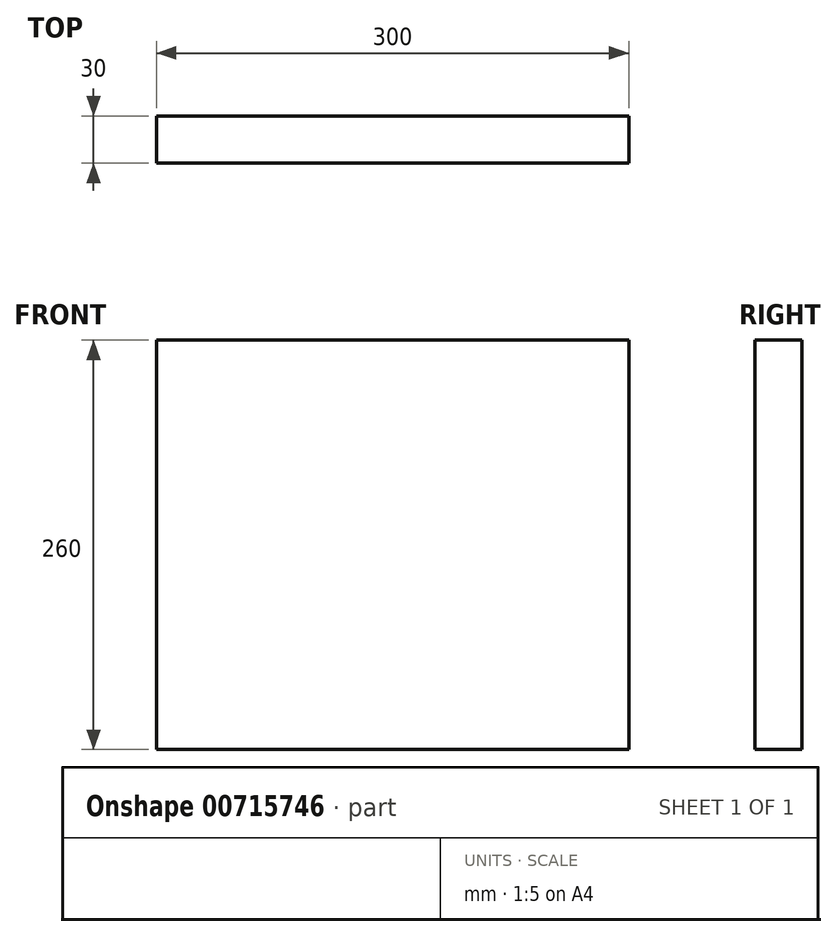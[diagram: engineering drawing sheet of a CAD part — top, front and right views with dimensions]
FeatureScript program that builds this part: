
annotation { "Feature Type Name" : "Feature", "Feature Type Description" : "" }
export const myFeature = defineFeature(function(context is Context, id is Id, definition is map)
    precondition{}
    {
        {
            var Q0;
            Q0=qCreatedBy(makeId("Front.planeOp"),FACE);
            var sketch = newSketch(context, id + "F0", { "sketchPlane" : qUnion([Q0])});
            skLineSegment(sketch, "E0.bottom", {"start": v(-150, 130) * mm, "end": v(150, 130) * mm});
            skLineSegment(sketch, "E0.top", {"start": v(-150, -130) * mm, "end": v(150, -130) * mm});
            skLineSegment(sketch, "E0.left", {"start": v(-150, 130) * mm, "end": v(-150, -130) * mm});
            skLineSegment(sketch, "E0.right", {"start": v(150, 130) * mm, "end": v(150, -130) * mm});
            skSolve(sketch);
        }
        {
            var Q0;
            Q0 = qSketchRegion(id + "F0", true);
            extrude(context, id + "F1", {"entities" : qUnion([Q0]), "depth" : 30 * mm, "offsetDistance" : 25 * mm});
        }
    });
